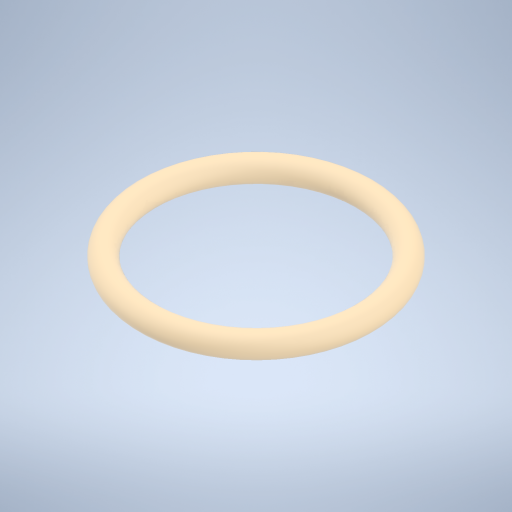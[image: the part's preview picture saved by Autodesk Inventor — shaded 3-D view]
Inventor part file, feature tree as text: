
AUTODESK INVENTOR PART (.ipt)
format: ipt  version: 2024.3 (Build 283343000, 343)  size: 279,040 bytes
history: native  units: mm
features: revolve x1, sketch x1
ambient origin geometry x8: Origin, YZ Plane, XZ Plane, XY Plane, X Axis, Y Axis, Z Axis, Center Point
bodies: Solid1 (feature_tree)
feature tree (2):
  revolve  "Revolution1"  [1 undecoded]
  sketch  "Sketch3"  dims[d3=0.5mm d4=2.35mm d5=90.0deg]
note: 1 required parameter value undecoded (feature->parameter linkage not recoverable at this tier; creation-order binding heuristic only, values carry confidence <= 0.55)
